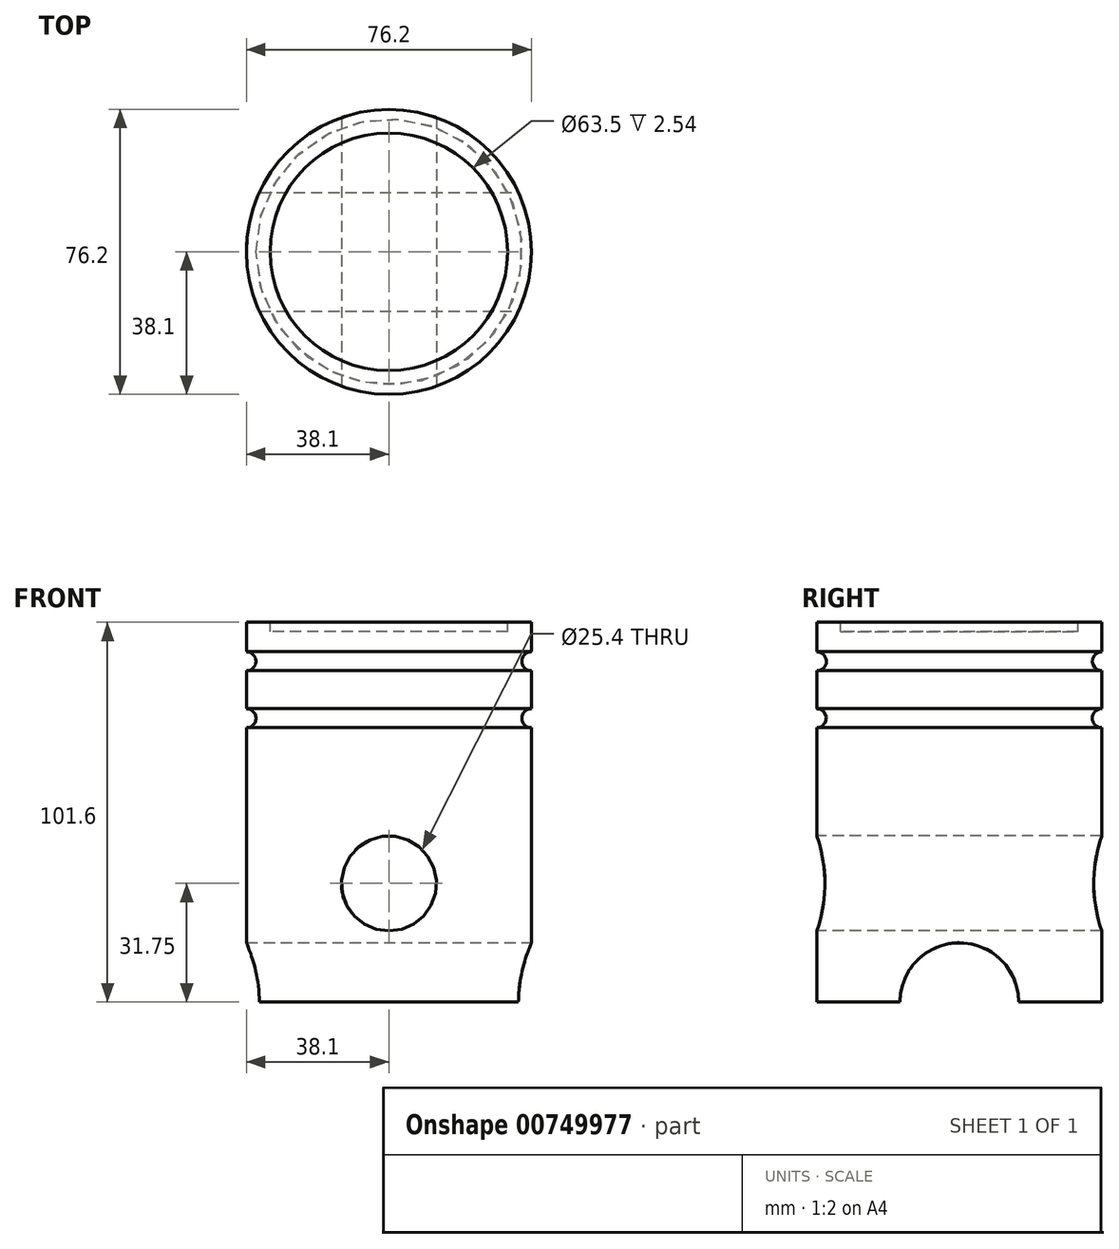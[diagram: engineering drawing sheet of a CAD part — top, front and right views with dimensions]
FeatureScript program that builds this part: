
annotation { "Feature Type Name" : "Feature", "Feature Type Description" : "" }
export const myFeature = defineFeature(function(context is Context, id is Id, definition is map)
    precondition{}
    {
        {
            var Q0;
            Q0=qCreatedBy(makeId("Top.planeOp"),FACE);
            var sketch = newSketch(context, id + "F0", { "sketchPlane" : qUnion([Q0])});
            skCircle(sketch, "E0", {"center": v(0, 0) * mm, "radius": 38.1 * mm});
            skSolve(sketch);
        }
        {
            var Q0;
            Q0 = qSketchRegion(id + "F0", true);
            extrude(context, id + "F1", {"entities" : qUnion([Q0]), "depth" : 101.6 * mm, "offsetDistance" : 25.4 * mm});
        }
        {
            var Q0;
            Q0=qCreatedBy(makeId("Front.planeOp"),FACE);
            var sketch = newSketch(context, id + "F2", { "sketchPlane" : qUnion([Q0])});
            skCircle(sketch, "E1", {"center": v(38.1, 91.17) * mm, "radius": 2.54 * mm});
            skPoint(sketch, "E2", {"position": v(0, 91.17) * mm});
            skSolve(sketch);
        }
        {
            var Q0;
            Q0 = qSketchRegion(id + "F2", true);
            var Q1;
            Q1=makeQuery(id+"F1.opExtrude","SWEPT_FACE",FACE,{"disambiguationData":[OSD([sQuery(id+"F0.wireOp",EDGE,"E0")])]});
            revolve(context, id + "F3", {"operationType" : NewBodyOperationType.REMOVE, "surfaceOperationType" : NewSurfaceOperationType.NEW, "entities" : qUnion([Q0]), "axis" : qUnion([Q1]), "revolveType" : RevolveType.FULL, "oppositeDirection" : true});
        }
        {
            var Q0;
            Q0=qCreatedBy(makeId("Front.planeOp"),FACE);
            var sketch = newSketch(context, id + "F4", { "sketchPlane" : qUnion([Q0])});
            skCircle(sketch, "E3", {"center": v(38.1, 75.93) * mm, "radius": 2.54 * mm});
            skPoint(sketch, "E4", {"position": v(0, 75.93) * mm});
            skSolve(sketch);
        }
        {
            var Q0;
            Q0 = qSketchRegion(id + "F4", true);
            var Q1;
            {var subQ0=sQuery(id+"F0.wireOp",EDGE,"E0");Q1=makeQuery(id+"F3.boolean.opBoolean","SPLIT",FACE,{"disambiguationData":[TD([makeQuery(id+"F1.opExtrude","CAP_FACE",FACE,{"disambiguationData":[OSD([subQ0])],"isStart":true})])],"derivedFrom":makeQuery(id+"F1.opExtrude","SWEPT_FACE",FACE,{"disambiguationData":[OSD([subQ0])]})});}
            revolve(context, id + "F5", {"operationType" : NewBodyOperationType.REMOVE, "surfaceOperationType" : NewSurfaceOperationType.NEW, "entities" : qUnion([Q0]), "axis" : qUnion([Q1]), "revolveType" : RevolveType.FULL, "oppositeDirection" : true});
        }
        {
            var Q0;
            Q0=qCreatedBy(makeId("Front.planeOp"),FACE);
            var sketch = newSketch(context, id + "F6", { "sketchPlane" : qUnion([Q0])});
            skCircle(sketch, "E5", {"center": v(0, 31.75) * mm, "radius": 12.7 * mm});
            skSolve(sketch);
        }
        {
            var Q0;
            Q0 = qSketchRegion(id + "F6", true);
            extrude(context, id + "F7", {"entities" : qUnion([Q0]), "operationType" : NewBodyOperationType.REMOVE, "endBound" : BoundingType.SYMMETRIC, "oppositeDirection" : true, "depth" : 101.6 * mm, "offsetDistance" : 25.4 * mm});
        }
        {
            var Q0;
            Q0=qCreatedBy(makeId("Right.planeOp"),FACE);
            var sketch = newSketch(context, id + "F8", { "sketchPlane" : qUnion([Q0])});
            skCircle(sketch, "E6", {"center": v(0, 0) * mm, "radius": 15.88 * mm});
            skSolve(sketch);
        }
        {
            var Q0;
            Q0 = qSketchRegion(id + "F8", true);
            extrude(context, id + "F9", {"entities" : qUnion([Q0]), "operationType" : NewBodyOperationType.REMOVE, "endBound" : BoundingType.SYMMETRIC, "oppositeDirection" : true, "depth" : 101.6 * mm, "offsetDistance" : 25.4 * mm});
        }
        {
            var Q0;
            Q0=qCreatedBy(makeId("Top.planeOp"),FACE);
            cPlane(context, id + "F10", {"entities" : qUnion([Q0]), "cplaneType" : CPlaneType.OFFSET, "offset" : 101.6 * mm, "width" : 152.4 * mm, "height" : 152.4 * mm});
        }
        {
            var Q0;
            Q0=qCreatedBy(id+"F10.planeOp",FACE);
            var sketch = newSketch(context, id + "F11", { "sketchPlane" : qUnion([Q0])});
            skCircle(sketch, "E7", {"center": v(0, 0) * mm, "radius": 31.75 * mm});
            skSolve(sketch);
        }
        {
            var Q0;
            Q0 = qSketchRegion(id + "F11", true);
            extrude(context, id + "F12", {"entities" : qUnion([Q0]), "operationType" : NewBodyOperationType.REMOVE, "oppositeDirection" : true, "depth" : 2.54 * mm, "offsetDistance" : 25.4 * mm});
        }
    });
